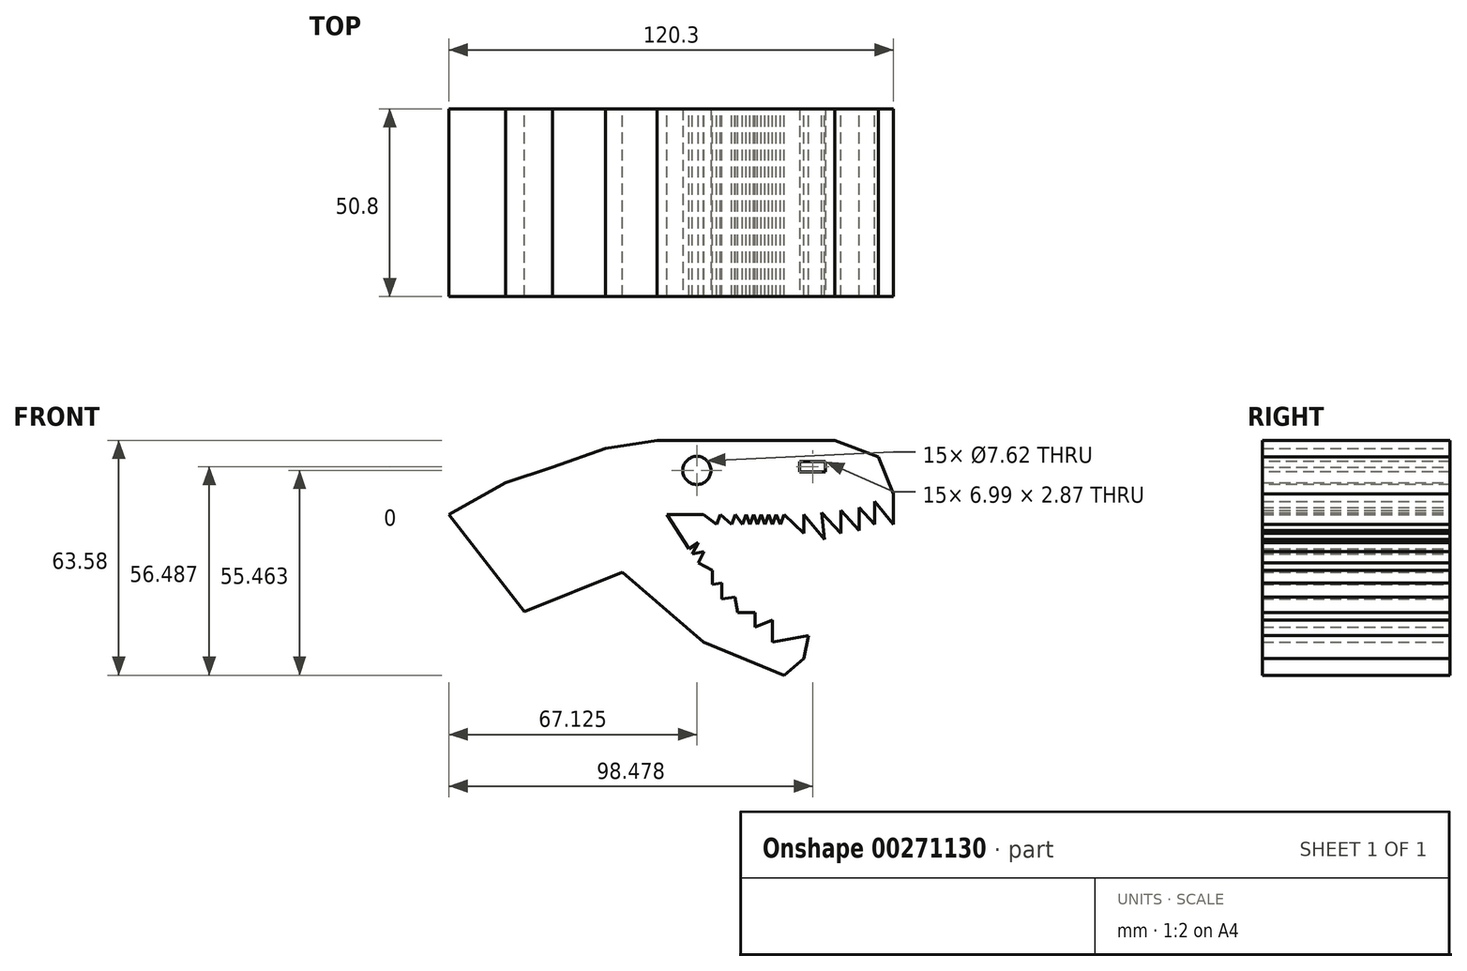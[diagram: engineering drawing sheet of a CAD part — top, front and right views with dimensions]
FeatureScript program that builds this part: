
annotation { "Feature Type Name" : "Feature", "Feature Type Description" : "" }
export const myFeature = defineFeature(function(context is Context, id is Id, definition is map)
    precondition{}
    {
        {
            var Q0;
            Q0=qCreatedBy(makeId("Front.planeOp"),FACE);
            var sketch = newSketch(context, id + "F0", { "sketchPlane" : qUnion([Q0])});
            skLineSegment(sketch, "E0", {"start": v(-47.55, 41.44) * mm, "end": v(-33.23, 46.6) * mm});
            skLineSegment(sketch, "E1", {"start": v(-33.23, 46.6) * mm, "end": v(-19.29, 48.7) * mm});
            skLineSegment(sketch, "E2", {"start": v(-19.29, 48.7) * mm, "end": v(28.83, 48.7) * mm});
            skLineSegment(sketch, "E3", {"start": v(28.83, 48.7) * mm, "end": v(40.67, 44.3) * mm});
            skLineSegment(sketch, "E4", {"start": v(40.67, 44.3) * mm, "end": v(44.68, 34.18) * mm});
            skLineSegment(sketch, "E5", {"start": v(44.68, 34.18) * mm, "end": v(34.53, 30.16) * mm});
            skLineSegment(sketch, "E6", {"start": v(34.53, 30.16) * mm, "end": v(20.43, 28.64) * mm});
            skLineSegment(sketch, "E7", {"start": v(20.43, 28.64) * mm, "end": v(-16.61, 28.64) * mm});
            skLineSegment(sketch, "E8", {"start": v(-16.61, 28.64) * mm, "end": v(-1.72, 5.73) * mm});
            skLineSegment(sketch, "E9", {"start": v(-1.72, 5.73) * mm, "end": v(12.03, -5.92) * mm});
            skLineSegment(sketch, "E10", {"start": v(12.03, -5.92) * mm, "end": v(20.43, -10.31) * mm});
            skLineSegment(sketch, "E11", {"start": v(20.43, -10.31) * mm, "end": v(15.09, -14.9) * mm});
            skLineSegment(sketch, "E12", {"start": v(15.09, -14.9) * mm, "end": v(-6.68, -5.92) * mm});
            skLineSegment(sketch, "E13", {"start": v(-6.68, -5.92) * mm, "end": v(-28.64, 12.98) * mm});
            skLineSegment(sketch, "E14", {"start": v(-28.64, 12.98) * mm, "end": v(-55.19, 2.3) * mm});
            skLineSegment(sketch, "E15", {"start": v(-55.19, 2.3) * mm, "end": v(-75.62, 28.64) * mm});
            skLineSegment(sketch, "E16", {"start": v(-75.62, 28.64) * mm, "end": v(-60.34, 37.24) * mm});
            skLineSegment(sketch, "E17", {"start": v(-60.34, 37.24) * mm, "end": v(-47.55, 41.44) * mm});
            skLineSegment(sketch, "E18", {"start": v(44.68, 34.18) * mm, "end": v(44.68, 25.97) * mm});
            skLineSegment(sketch, "E19", {"start": v(44.68, 25.97) * mm, "end": v(39.6, 32.17) * mm});
            skLineSegment(sketch, "E20", {"start": v(39.6, 32.17) * mm, "end": v(39.6, 25.97) * mm});
            skLineSegment(sketch, "E21", {"start": v(39.6, 25.97) * mm, "end": v(35.52, 30.55) * mm});
            skLineSegment(sketch, "E22", {"start": v(35.52, 30.55) * mm, "end": v(35.52, 24.25) * mm});
            skLineSegment(sketch, "E23", {"start": v(35.52, 24.25) * mm, "end": v(30.46, 29.72) * mm});
            skLineSegment(sketch, "E24", {"start": v(30.46, 29.72) * mm, "end": v(30.46, 23.49) * mm});
            skLineSegment(sketch, "E25", {"start": v(30.46, 23.49) * mm, "end": v(25.34, 29.17) * mm});
            skLineSegment(sketch, "E26", {"start": v(25.34, 29.17) * mm, "end": v(26.12, 21.89) * mm});
            skLineSegment(sketch, "E27", {"start": v(26.12, 21.89) * mm, "end": v(20.43, 28.64) * mm});
            skLineSegment(sketch, "E28", {"start": v(20.43, 23.49) * mm, "end": v(20.43, 28.64) * mm});
            skLineSegment(sketch, "E29", {"start": v(20.43, 23.49) * mm, "end": v(15.09, 28.64) * mm});
            skLineSegment(sketch, "E30", {"start": v(15.09, 28.64) * mm, "end": v(14.1, 25.97) * mm});
            skLineSegment(sketch, "E31", {"start": v(14.1, 25.97) * mm, "end": v(13.03, 28.64) * mm});
            skLineSegment(sketch, "E32", {"start": v(13.03, 28.64) * mm, "end": v(12.03, 25.94) * mm});
            skLineSegment(sketch, "E33", {"start": v(12.03, 25.94) * mm, "end": v(10.96, 28.64) * mm});
            skLineSegment(sketch, "E34", {"start": v(10.96, 28.64) * mm, "end": v(9.97, 25.97) * mm});
            skLineSegment(sketch, "E35", {"start": v(9.97, 25.97) * mm, "end": v(8.9, 28.64) * mm});
            skLineSegment(sketch, "E36", {"start": v(8.9, 28.64) * mm, "end": v(7.91, 25.97) * mm});
            skLineSegment(sketch, "E37", {"start": v(7.91, 25.97) * mm, "end": v(6.86, 28.64) * mm});
            skLineSegment(sketch, "E38", {"start": v(6.86, 28.64) * mm, "end": v(5.86, 25.97) * mm});
            skLineSegment(sketch, "E39", {"start": v(5.86, 25.97) * mm, "end": v(4.8, 28.64) * mm});
            skLineSegment(sketch, "E40", {"start": v(4.8, 28.64) * mm, "end": v(3.81, 25.97) * mm});
            skLineSegment(sketch, "E41", {"start": v(3.81, 25.97) * mm, "end": v(1.9, 28.64) * mm});
            skLineSegment(sketch, "E42", {"start": v(1.9, 28.64) * mm, "end": v(0.92, 25.97) * mm});
            skLineSegment(sketch, "E43", {"start": v(0.92, 25.97) * mm, "end": v(-2.1, 28.64) * mm});
            skLineSegment(sketch, "E44", {"start": v(-2.1, 28.64) * mm, "end": v(-3.1, 25.97) * mm});
            skLineSegment(sketch, "E45", {"start": v(-3.1, 25.97) * mm, "end": v(-6.68, 28.64) * mm});
            skLineSegment(sketch, "E46", {"start": v(20.43, -10.31) * mm, "end": v(21.77, -4.2) * mm});
            skLineSegment(sketch, "E47", {"start": v(21.77, -4.2) * mm, "end": v(12.03, -5.92) * mm});
            skLineSegment(sketch, "E48", {"start": v(12.03, -5.92) * mm, "end": v(12.03, 0) * mm});
            skLineSegment(sketch, "E49", {"start": v(12.03, 0) * mm, "end": v(7.23, -1.85) * mm});
            skLineSegment(sketch, "E50", {"start": v(7.23, -1.85) * mm, "end": v(7.23, 2.1) * mm});
            skLineSegment(sketch, "E51", {"start": v(7.23, 2.1) * mm, "end": v(2.56, 2.1) * mm});
            skLineSegment(sketch, "E52", {"start": v(2.56, 2.1) * mm, "end": v(1.82, 6.32) * mm});
            skLineSegment(sketch, "E53", {"start": v(1.82, 6.32) * mm, "end": v(-1.72, 5.73) * mm});
            skLineSegment(sketch, "E54", {"start": v(-1.72, 10.12) * mm, "end": v(-4.28, 9.67) * mm});
            skLineSegment(sketch, "E55", {"start": v(-4.28, 9.67) * mm, "end": v(-1.72, 10.12) * mm});
            skLineSegment(sketch, "E56", {"start": v(-1.72, 5.73) * mm, "end": v(-1.72, 10.12) * mm});
            skLineSegment(sketch, "E57", {"start": v(-4.28, 9.67) * mm, "end": v(-4.28, 13.56) * mm});
            skLineSegment(sketch, "E58", {"start": v(-4.28, 13.56) * mm, "end": v(-8.1, 15.56) * mm});
            skLineSegment(sketch, "E59", {"start": v(-8.1, 15.56) * mm, "end": v(-6.55, 18.55) * mm});
            skLineSegment(sketch, "E60", {"start": v(-6.55, 18.55) * mm, "end": v(-9.7, 18) * mm});
            skLineSegment(sketch, "E61", {"start": v(-9.7, 18) * mm, "end": v(-8.1, 21.02) * mm});
            skLineSegment(sketch, "E62", {"start": v(-8.1, 21.02) * mm, "end": v(-10.6, 19.4) * mm});
            skSolve(sketch);
        }
        {
            var Q0;
            Q0 = qSketchRegion(id + "F0", true);
            extrude(context, id + "F1", {"entities" : qUnion([Q0]), "depth" : 50.8 * mm});
        }
        {
            var Q0;
            Q0=makeQuery(id+"F1.opExtrude","CAP_FACE",FACE,{"disambiguationData":[OSD([sQuery(id+"F0.wireOp",EDGE,"E0"),sQuery(id+"F0.wireOp",EDGE,"E1"),sQuery(id+"F0.wireOp",EDGE,"E2"),sQuery(id+"F0.wireOp",EDGE,"E3"),sQuery(id+"F0.wireOp",EDGE,"E4"),sQuery(id+"F0.wireOp",EDGE,"E7"),sQuery(id+"F0.wireOp",EDGE,"E8"),sQuery(id+"F0.wireOp",EDGE,"E11"),sQuery(id+"F0.wireOp",EDGE,"E12"),sQuery(id+"F0.wireOp",EDGE,"E13"),sQuery(id+"F0.wireOp",EDGE,"E14"),sQuery(id+"F0.wireOp",EDGE,"E15"),sQuery(id+"F0.wireOp",EDGE,"E16"),sQuery(id+"F0.wireOp",EDGE,"E17"),sQuery(id+"F0.wireOp",EDGE,"E18"),sQuery(id+"F0.wireOp",EDGE,"E19"),sQuery(id+"F0.wireOp",EDGE,"E20"),sQuery(id+"F0.wireOp",EDGE,"E21"),sQuery(id+"F0.wireOp",EDGE,"E22"),sQuery(id+"F0.wireOp",EDGE,"E23"),sQuery(id+"F0.wireOp",EDGE,"E24"),sQuery(id+"F0.wireOp",EDGE,"E25"),sQuery(id+"F0.wireOp",EDGE,"E26"),sQuery(id+"F0.wireOp",EDGE,"E27"),sQuery(id+"F0.wireOp",EDGE,"E28"),sQuery(id+"F0.wireOp",EDGE,"E29"),sQuery(id+"F0.wireOp",EDGE,"E30"),sQuery(id+"F0.wireOp",EDGE,"E31"),sQuery(id+"F0.wireOp",EDGE,"E32"),sQuery(id+"F0.wireOp",EDGE,"E33"),sQuery(id+"F0.wireOp",EDGE,"E34"),sQuery(id+"F0.wireOp",EDGE,"E35"),sQuery(id+"F0.wireOp",EDGE,"E36"),sQuery(id+"F0.wireOp",EDGE,"E37"),sQuery(id+"F0.wireOp",EDGE,"E38"),sQuery(id+"F0.wireOp",EDGE,"E39"),sQuery(id+"F0.wireOp",EDGE,"E40"),sQuery(id+"F0.wireOp",EDGE,"E41"),sQuery(id+"F0.wireOp",EDGE,"E42"),sQuery(id+"F0.wireOp",EDGE,"E43"),sQuery(id+"F0.wireOp",EDGE,"E44"),sQuery(id+"F0.wireOp",EDGE,"E45"),sQuery(id+"F0.wireOp",EDGE,"E46"),sQuery(id+"F0.wireOp",EDGE,"E47"),sQuery(id+"F0.wireOp",EDGE,"E48"),sQuery(id+"F0.wireOp",EDGE,"E49"),sQuery(id+"F0.wireOp",EDGE,"E50"),sQuery(id+"F0.wireOp",EDGE,"E51"),sQuery(id+"F0.wireOp",EDGE,"E52"),sQuery(id+"F0.wireOp",EDGE,"E53"),sQuery(id+"F0.wireOp",EDGE,"E55"),sQuery(id+"F0.wireOp",EDGE,"E56"),sQuery(id+"F0.wireOp",EDGE,"E57"),sQuery(id+"F0.wireOp",EDGE,"E58"),sQuery(id+"F0.wireOp",EDGE,"E59"),sQuery(id+"F0.wireOp",EDGE,"E60"),sQuery(id+"F0.wireOp",EDGE,"E61"),sQuery(id+"F0.wireOp",EDGE,"E62")])],"isStart":false});
            var sketch = newSketch(context, id + "F2", { "sketchPlane" : qUnion([Q0])});
            skLineSegment(sketch, "E63.bottom", {"start": v(26.35, 40.16) * mm, "end": v(19.36, 40.16) * mm});
            skLineSegment(sketch, "E63.top", {"start": v(26.35, 43.03) * mm, "end": v(19.36, 43.03) * mm});
            skLineSegment(sketch, "E63.left", {"start": v(26.35, 40.16) * mm, "end": v(26.35, 43.03) * mm});
            skLineSegment(sketch, "E63.right", {"start": v(19.36, 40.16) * mm, "end": v(19.36, 43.03) * mm});
            skSolve(sketch);
        }
        {
            var Q0;
            Q0=makeQuery(id+"F2.imprint","IMPRINT",FACE,{"disambiguationData":[TD([[makeQuery(id+"F2.imprint","IMPRINT",EDGE,{"derivedFrom":sQuery(id+"F2.wireOp",EDGE,"E63.bottom")}),-1.0]])]});
            extrude(context, id + "F3", {"entities" : qUnion([Q0]), "operationType" : NewBodyOperationType.REMOVE, "oppositeDirection" : true, "depth" : 50.8 * mm});
        }
        {
            var Q0;
            Q0=makeQuery(id+"F1.opExtrude","CAP_FACE",FACE,{"disambiguationData":[OSD([sQuery(id+"F0.wireOp",EDGE,"E0"),sQuery(id+"F0.wireOp",EDGE,"E1"),sQuery(id+"F0.wireOp",EDGE,"E2"),sQuery(id+"F0.wireOp",EDGE,"E3"),sQuery(id+"F0.wireOp",EDGE,"E4"),sQuery(id+"F0.wireOp",EDGE,"E7"),sQuery(id+"F0.wireOp",EDGE,"E8"),sQuery(id+"F0.wireOp",EDGE,"E11"),sQuery(id+"F0.wireOp",EDGE,"E12"),sQuery(id+"F0.wireOp",EDGE,"E13"),sQuery(id+"F0.wireOp",EDGE,"E14"),sQuery(id+"F0.wireOp",EDGE,"E15"),sQuery(id+"F0.wireOp",EDGE,"E16"),sQuery(id+"F0.wireOp",EDGE,"E17"),sQuery(id+"F0.wireOp",EDGE,"E18"),sQuery(id+"F0.wireOp",EDGE,"E19"),sQuery(id+"F0.wireOp",EDGE,"E20"),sQuery(id+"F0.wireOp",EDGE,"E21"),sQuery(id+"F0.wireOp",EDGE,"E22"),sQuery(id+"F0.wireOp",EDGE,"E23"),sQuery(id+"F0.wireOp",EDGE,"E24"),sQuery(id+"F0.wireOp",EDGE,"E25"),sQuery(id+"F0.wireOp",EDGE,"E26"),sQuery(id+"F0.wireOp",EDGE,"E27"),sQuery(id+"F0.wireOp",EDGE,"E28"),sQuery(id+"F0.wireOp",EDGE,"E29"),sQuery(id+"F0.wireOp",EDGE,"E30"),sQuery(id+"F0.wireOp",EDGE,"E31"),sQuery(id+"F0.wireOp",EDGE,"E32"),sQuery(id+"F0.wireOp",EDGE,"E33"),sQuery(id+"F0.wireOp",EDGE,"E34"),sQuery(id+"F0.wireOp",EDGE,"E35"),sQuery(id+"F0.wireOp",EDGE,"E36"),sQuery(id+"F0.wireOp",EDGE,"E37"),sQuery(id+"F0.wireOp",EDGE,"E38"),sQuery(id+"F0.wireOp",EDGE,"E39"),sQuery(id+"F0.wireOp",EDGE,"E40"),sQuery(id+"F0.wireOp",EDGE,"E41"),sQuery(id+"F0.wireOp",EDGE,"E42"),sQuery(id+"F0.wireOp",EDGE,"E43"),sQuery(id+"F0.wireOp",EDGE,"E44"),sQuery(id+"F0.wireOp",EDGE,"E45"),sQuery(id+"F0.wireOp",EDGE,"E46"),sQuery(id+"F0.wireOp",EDGE,"E47"),sQuery(id+"F0.wireOp",EDGE,"E48"),sQuery(id+"F0.wireOp",EDGE,"E49"),sQuery(id+"F0.wireOp",EDGE,"E50"),sQuery(id+"F0.wireOp",EDGE,"E51"),sQuery(id+"F0.wireOp",EDGE,"E52"),sQuery(id+"F0.wireOp",EDGE,"E53"),sQuery(id+"F0.wireOp",EDGE,"E55"),sQuery(id+"F0.wireOp",EDGE,"E56"),sQuery(id+"F0.wireOp",EDGE,"E57"),sQuery(id+"F0.wireOp",EDGE,"E58"),sQuery(id+"F0.wireOp",EDGE,"E59"),sQuery(id+"F0.wireOp",EDGE,"E60"),sQuery(id+"F0.wireOp",EDGE,"E61"),sQuery(id+"F0.wireOp",EDGE,"E62")])],"isStart":false});
            var sketch = newSketch(context, id + "F4", { "sketchPlane" : qUnion([Q0])});
            skCircle(sketch, "E64", {"center": v(-8.5, 40.57) * mm, "radius": 3.81 * mm});
            skSolve(sketch);
        }
        {
            var Q0;
            Q0 = qSketchRegion(id + "F4", true);
            extrude(context, id + "F5", {"entities" : qUnion([Q0]), "operationType" : NewBodyOperationType.REMOVE, "oppositeDirection" : true, "depth" : 50.8 * mm});
        }
    });
